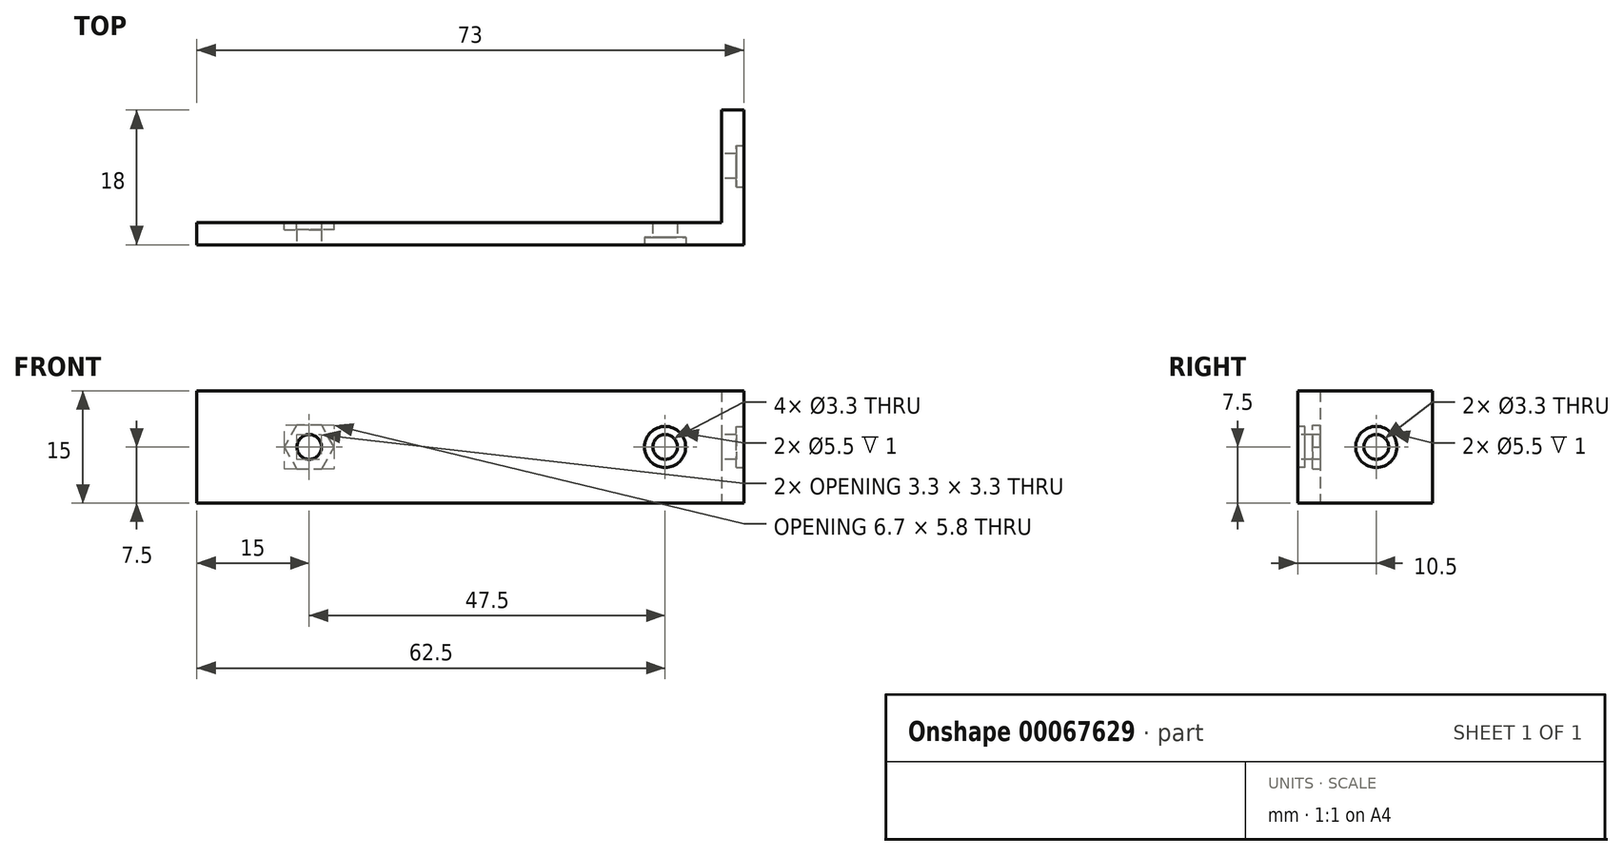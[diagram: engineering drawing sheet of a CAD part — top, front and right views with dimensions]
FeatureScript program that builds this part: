
annotation { "Feature Type Name" : "Feature", "Feature Type Description" : "" }
export const myFeature = defineFeature(function(context is Context, id is Id, definition is map)
    precondition{}
    {
        {
            var Q0;
            Q0=qCreatedBy(makeId("Top.planeOp"),FACE);
            var sketch = newSketch(context, id + "F0", { "sketchPlane" : qUnion([Q0])});
            skLineSegment(sketch, "E0.rect.bottom", {"start": v(-35, 1.5) * mm, "end": v(35, 1.5) * mm});
            skLineSegment(sketch, "E0.rect.top", {"start": v(-35, -1.5) * mm, "end": v(35, -1.5) * mm});
            skLineSegment(sketch, "E0.rect.left", {"start": v(-35, 1.5) * mm, "end": v(-35, -1.5) * mm});
            skLineSegment(sketch, "E0.rect.right", {"start": v(35, 1.5) * mm, "end": v(35, -1.5) * mm});
            skPoint(sketch, "E0.rect.middle", {"position": v(0, 0) * mm});
            skLineSegment(sketch, "E1.bottom", {"start": v(35, -1.5) * mm, "end": v(38, -1.5) * mm});
            skLineSegment(sketch, "E1.top", {"start": v(35, 16.5) * mm, "end": v(38, 16.5) * mm});
            skLineSegment(sketch, "E1.left", {"start": v(35, -1.5) * mm, "end": v(35, 16.5) * mm});
            skLineSegment(sketch, "E1.right", {"start": v(38, -1.5) * mm, "end": v(38, 16.5) * mm});
            skSolve(sketch);
        }
        {
            var Q0;
            {var subQ0=sQuery(id+"F0.wireOp",EDGE,"E0.rect.bottom");Q0=makeQuery(id+"F0.imprint","IMPRINT",FACE,{"disambiguationData":[TD([[makeQuery(id+"F0.imprint","IMPRINT",EDGE,{"derivedFrom":subQ0}),-1.0]])]});}
            var Q1;
            {var subQ3=sQuery(id+"F0.wireOp",EDGE,"E1.bottom");Q1=makeQuery(id+"F0.imprint","IMPRINT",FACE,{"disambiguationData":[TD([[makeQuery(id+"F0.imprint","IMPRINT",EDGE,{"derivedFrom":subQ3}),1.0]])]});}
            extrude(context, id + "F1", {"entities" : qUnion([Q0, Q1]), "depth" : 15 * mm});
        }
        {
            var Q0;
            Q0=makeQuery(id+"F1.opExtrude","SWEPT_FACE",FACE,{"disambiguationData":[OSD([sQuery(id+"F0.wireOp",EDGE,"E1.left")])]});
            var sketch = newSketch(context, id + "F2", { "sketchPlane" : qUnion([Q0])});
            skCircle(sketch, "E2", {"center": v(-9, 7.5) * mm, "radius": 1.65 * mm});
            skSolve(sketch);
        }
        {
            var Q0;
            Q0=makeQuery(id+"F2.imprint","IMPRINT",FACE,{"disambiguationData":[TD([[makeQuery(id+"F2.imprint","IMPRINT",EDGE,{"derivedFrom":sQuery(id+"F2.wireOp",EDGE,"E2")}),1.0]])]});
            extrude(context, id + "F3", {"entities" : qUnion([Q0]), "operationType" : NewBodyOperationType.REMOVE, "oppositeDirection" : true, "depth" : 25 * mm});
        }
        {
            var Q0;
            Q0=makeQuery(id+"F1.opExtrude","SWEPT_FACE",FACE,{"disambiguationData":[OSD([sQuery(id+"F0.wireOp",EDGE,"E1.right")])]});
            var sketch = newSketch(context, id + "F4", { "sketchPlane" : qUnion([Q0])});
            skCircle(sketch, "E3", {"center": v(9, 7.5) * mm, "radius": 2.75 * mm});
            skSolve(sketch);
        }
        {
            var Q0;
            Q0=makeQuery(id+"F4.imprint","IMPRINT",FACE,{"disambiguationData":[TD([[makeQuery(id+"F4.imprint","IMPRINT",EDGE,{"derivedFrom":sQuery(id+"F4.wireOp",EDGE,"E3")}),1.0]])]});
            extrude(context, id + "F5", {"entities" : qUnion([Q0]), "operationType" : NewBodyOperationType.REMOVE, "oppositeDirection" : true, "depth" : 1 * mm});
        }
        {
            var Q0;
            Q0=makeQuery(id+"F1.opExtrude","SWEPT_FACE",FACE,{"disambiguationData":[OSD([sQuery(id+"F0.wireOp",EDGE,"E0.rect.top"),sQuery(id+"F0.wireOp",EDGE,"E1.bottom")])]});
            var sketch = newSketch(context, id + "F6", { "sketchPlane" : qUnion([Q0])});
            skCircle(sketch, "E4", {"center": v(-20, 7.5) * mm, "radius": 1.65 * mm});
            skSolve(sketch);
        }
        {
            var Q0;
            Q0=makeQuery(id+"F6.imprint","IMPRINT",FACE,{"disambiguationData":[TD([[makeQuery(id+"F6.imprint","IMPRINT",EDGE,{"derivedFrom":sQuery(id+"F6.wireOp",EDGE,"E4")}),1.0]])]});
            extrude(context, id + "F7", {"entities" : qUnion([Q0]), "operationType" : NewBodyOperationType.REMOVE, "endBound" : BoundingType.UP_TO_NEXT, "oppositeDirection" : true, "depth" : 25 * mm});
        }
        {
            var Q0;
            Q0=makeQuery(id+"F1.opExtrude","SWEPT_FACE",FACE,{"disambiguationData":[OSD([sQuery(id+"F0.wireOp",EDGE,"E0.rect.top"),sQuery(id+"F0.wireOp",EDGE,"E1.bottom")])]});
            var sketch = newSketch(context, id + "F8", { "sketchPlane" : qUnion([Q0])});
            skCircle(sketch, "E5", {"center": v(27.5, 7.5) * mm, "radius": 2.75 * mm});
            skCircle(sketch, "E6", {"center": v(27.5, 7.5) * mm, "radius": 1.65 * mm});
            skSolve(sketch);
        }
        {
            var Q0;
            Q0=makeQuery(id+"F8.imprint","IMPRINT",FACE,{"disambiguationData":[TD([[makeQuery(id+"F8.imprint","IMPRINT",EDGE,{"derivedFrom":sQuery(id+"F8.wireOp",EDGE,"E6")}),1.0]])]});
            extrude(context, id + "F9", {"entities" : qUnion([Q0]), "operationType" : NewBodyOperationType.REMOVE, "endBound" : BoundingType.UP_TO_NEXT, "oppositeDirection" : true, "depth" : 25 * mm});
        }
        {
            var Q0;
            Q0=makeQuery(id+"F8.imprint","IMPRINT",FACE,{"disambiguationData":[TD([[makeQuery(id+"F8.imprint","IMPRINT",EDGE,{"derivedFrom":sQuery(id+"F8.wireOp",EDGE,"E5")}),1.0]])]});
            extrude(context, id + "F10", {"entities" : qUnion([Q0]), "operationType" : NewBodyOperationType.REMOVE, "oppositeDirection" : true, "depth" : 1 * mm});
        }
        {
            var Q0;
            Q0=makeQuery(id+"F1.opExtrude","SWEPT_FACE",FACE,{"disambiguationData":[OSD([sQuery(id+"F0.wireOp",EDGE,"E0.rect.bottom")])]});
            var sketch = newSketch(context, id + "F11", { "sketchPlane" : qUnion([Q0])});
            skCircle(sketch, "E7.cCircle", {"center": v(20, 7.5) * mm, "radius": 2.9 * mm, "construction": true});
            skLineSegment(sketch, "E7.0", {"start": v(18.33, 10.4) * mm, "end": v(21.67, 10.4) * mm});
            skLineSegment(sketch, "E7.1", {"start": v(21.67, 10.4) * mm, "end": v(23.35, 7.5) * mm});
            skLineSegment(sketch, "E7.2", {"start": v(23.35, 7.5) * mm, "end": v(21.67, 4.6) * mm});
            skLineSegment(sketch, "E7.3", {"start": v(21.67, 4.6) * mm, "end": v(18.33, 4.6) * mm});
            skLineSegment(sketch, "E7.4", {"start": v(18.33, 4.6) * mm, "end": v(16.65, 7.5) * mm});
            skLineSegment(sketch, "E7.5", {"start": v(16.65, 7.5) * mm, "end": v(18.33, 10.4) * mm});
            skPoint(sketch, "E7.0.midPoint", {"position": v(20, 10.4) * mm});
            skSolve(sketch);
        }
        {
            var Q0;
            Q0=makeQuery(id+"F11.imprint","IMPRINT",FACE,{"disambiguationData":[TD([[makeQuery(id+"F11.imprint","IMPRINT",EDGE,{"derivedFrom":sQuery(id+"F11.wireOp",EDGE,"E7.0")}),-1.0]])]});
            extrude(context, id + "F12", {"entities" : qUnion([Q0]), "operationType" : NewBodyOperationType.REMOVE, "oppositeDirection" : true, "depth" : 1 * mm});
        }
    });
